# Revit family: SPRINKLER 2500
name_source: partatom
category: Sprinklers
units: mm (PartAtom-declared; Revit-internal decimal feet)

## family parameters
Always vertical = No
Cut with Voids When Loaded = Yes
Maintain Annotation Orientation = No
Part Type = Normal
Room Calculation Point = No
Round Connector Dimension = Use Diameter
Shared = No
Work Plane-Based = No

## types (5) — shared parameters
A = 52 mm
Default Elevation = 1219 mm
Manufacturer = INKA
Model = Preasure Plate With Square Bolt
Preasure Plate With
Revit Designer = DEKO Group
URL = http://www.inkafixing.com
d = 4 mm  [stored 0.0131234 ft]

## per-type parameters (varying)
| type | B | Code No |
| IFMFC0889 | 72 mm | IFMFC0889 |
| IFMFC08109 | 109 mm  [stored 0.357612 ft] | IFMFC08109 |
| IFMFC0889 2-300 2 KOLLU | 72 mm | IFMFC0889 |
| IFMFC0889 2-300 | 72 mm | IFMFC0889 |
| IFMFC0889 2tekli | 72 mm | IFMFC0889 |

note: [stored X ft] marks values corroborated as IEEE doubles in the binary element streams (Revit-internal decimal feet)

## geometry (parser evidence)
native form markers: Sweep x4
no freeform markers — native parametric forms only
